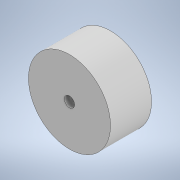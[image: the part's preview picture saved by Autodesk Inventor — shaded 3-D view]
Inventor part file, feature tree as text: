
AUTODESK INVENTOR PART (.ipt)
format: ipt  version: 2020.1 (Build 241239000, 239)  size: 97,792 bytes
history: native  units: mm
features: extrude x1, sketch x1
ambient origin geometry x8: Origin, YZ Plane, XZ Plane, XY Plane, X Axis, Y Axis, Z Axis, Center Point
bodies: Solid1 (feature_tree)
feature tree (2):
  extrude  "Extrusion1"  Depth=48.0mm
  sketch  "Sketch1"  dims[d0=96.0mm d1=12.0mm d2=48.0mm d3=0.0mm]
